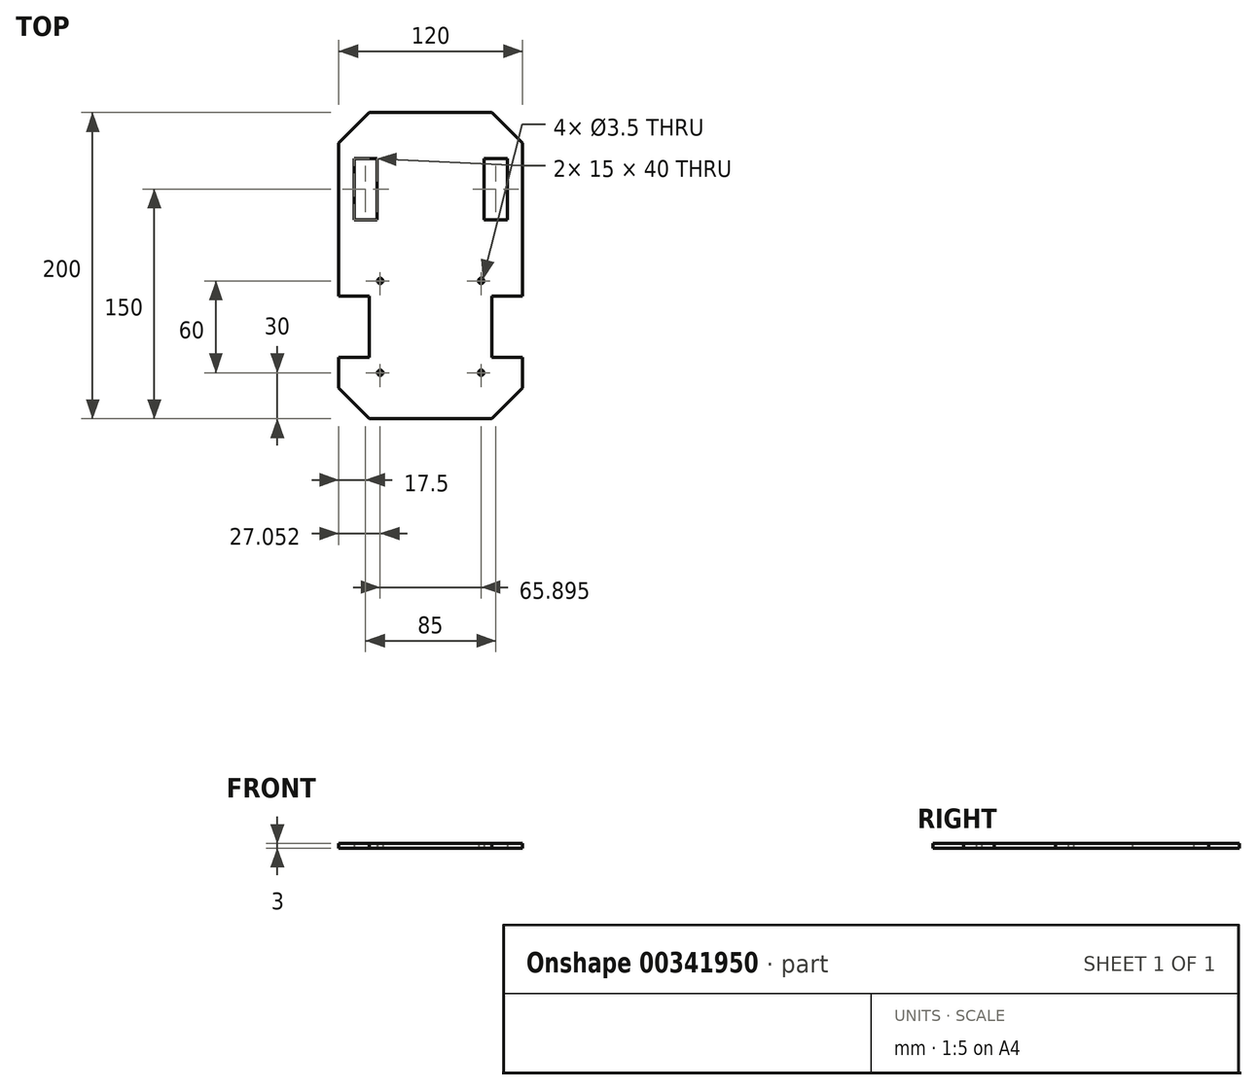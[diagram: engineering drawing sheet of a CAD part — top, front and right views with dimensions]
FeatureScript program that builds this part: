
annotation { "Feature Type Name" : "Feature", "Feature Type Description" : "" }
export const myFeature = defineFeature(function(context is Context, id is Id, definition is map)
    precondition{}
    {
        {
            var Q0;
            Q0=qCreatedBy(makeId("Top.planeOp"),FACE);
            var sketch = newSketch(context, id + "F0", { "sketchPlane" : qUnion([Q0])});
            skLineSegment(sketch, "E0.bottom", {"start": v(20, 0) * mm, "end": v(60, 0) * mm});
            skLineSegment(sketch, "E0.top", {"start": v(20, 200) * mm, "end": v(60, 200) * mm});
            skLineSegment(sketch, "E0.left", {"start": v(0, 20) * mm, "end": v(0, 40) * mm});
            skLineSegment(sketch, "E0.right", {"start": v(60, 0) * mm, "end": v(60, 200) * mm, "construction": true});
            skLineSegment(sketch, "E1.bottom", {"start": v(0, 80) * mm, "end": v(20, 80) * mm});
            skLineSegment(sketch, "E1.top", {"start": v(0, 40) * mm, "end": v(20, 40) * mm});
            skLineSegment(sketch, "E1.right", {"start": v(20, 80) * mm, "end": v(20, 40) * mm});
            skLineSegment(sketch, "E2.trimOffspring", {"start": v(0, 80) * mm, "end": v(0, 180) * mm});
            skLineSegment(sketch, "E3", {"start": v(0, 20) * mm, "end": v(20, 0) * mm});
            skPoint(sketch, "E4.orphan", {"position": v(0, 0) * mm});
            skCircle(sketch, "E5", {"center": v(27.05, 30) * mm, "radius": 1.75 * mm});
            skLineSegment(sketch, "E6", {"start": v(20, 60) * mm, "end": v(39.86, 60) * mm, "construction": true});
            skPoint(sketch, "E6.endSnap0", {"position": v(20, 60) * mm});
            skCircle(sketch, "E7.MirrorC", {"center": v(27.05, 90) * mm, "radius": 1.75 * mm});
            skLineSegment(sketch, "E8.bottom", {"start": v(10, 170) * mm, "end": v(25, 170) * mm});
            skLineSegment(sketch, "E8.top", {"start": v(10, 130) * mm, "end": v(25, 130) * mm});
            skLineSegment(sketch, "E8.left", {"start": v(10, 170) * mm, "end": v(10, 130) * mm});
            skLineSegment(sketch, "E8.right", {"start": v(25, 170) * mm, "end": v(25, 130) * mm});
            skLineSegment(sketch, "E9", {"start": v(20, 200) * mm, "end": v(0, 180) * mm});
            skCircle(sketch, "E10.MirrorC", {"center": v(92.95, 90) * mm, "radius": 1.75 * mm});
            skCircle(sketch, "E11.MirrorC", {"center": v(92.95, 30) * mm, "radius": 1.75 * mm});
            skLineSegment(sketch, "E12.MirrorCS", {"start": v(110, 130) * mm, "end": v(95, 130) * mm});
            skLineSegment(sketch, "E13.MirrorCS", {"start": v(110, 170) * mm, "end": v(110, 130) * mm});
            skPoint(sketch, "E14.MirrorP", {"position": v(100, 60) * mm});
            skLineSegment(sketch, "E15.MirrorCS", {"start": v(110, 170) * mm, "end": v(95, 170) * mm});
            skLineSegment(sketch, "E16.MirrorCS", {"start": v(100, 60) * mm, "end": v(80.14, 60) * mm, "construction": true});
            skLineSegment(sketch, "E17.MirrorCS", {"start": v(95, 170) * mm, "end": v(95, 130) * mm});
            skLineSegment(sketch, "E18.MirrorCS", {"start": v(120, 40) * mm, "end": v(100, 40) * mm});
            skLineSegment(sketch, "E19.MirrorCS", {"start": v(120, 80) * mm, "end": v(100, 80) * mm});
            skLineSegment(sketch, "E20.MirrorCS", {"start": v(100, 200) * mm, "end": v(120, 180) * mm});
            skLineSegment(sketch, "E21.MirrorCS", {"start": v(100, 80) * mm, "end": v(100, 40) * mm});
            skLineSegment(sketch, "E22.MirrorCS", {"start": v(120, 20) * mm, "end": v(120, 40) * mm});
            skLineSegment(sketch, "E23.MirrorCS", {"start": v(120, 20) * mm, "end": v(100, 0) * mm});
            skLineSegment(sketch, "E24.MirrorCS", {"start": v(100, 0) * mm, "end": v(60, 0) * mm});
            skPoint(sketch, "E25.MirrorP", {"position": v(120, 0) * mm});
            skLineSegment(sketch, "E26.MirrorCS", {"start": v(120, 80) * mm, "end": v(120, 180) * mm});
            skLineSegment(sketch, "E27.MirrorCS", {"start": v(100, 200) * mm, "end": v(60, 200) * mm});
            skSolve(sketch);
        }
        {
            var Q0;
            Q0=makeQuery(id+"F0.imprint","IMPRINT",FACE,{"disambiguationData":[TD([[makeQuery(id+"F0.imprint","IMPRINT",EDGE,{"derivedFrom":sQuery(id+"F0.wireOp",EDGE,"E0.bottom")}),1.0]])]});
            extrude(context, id + "F1", {"entities" : qUnion([Q0]), "depth" : 3 * mm});
        }
    });
